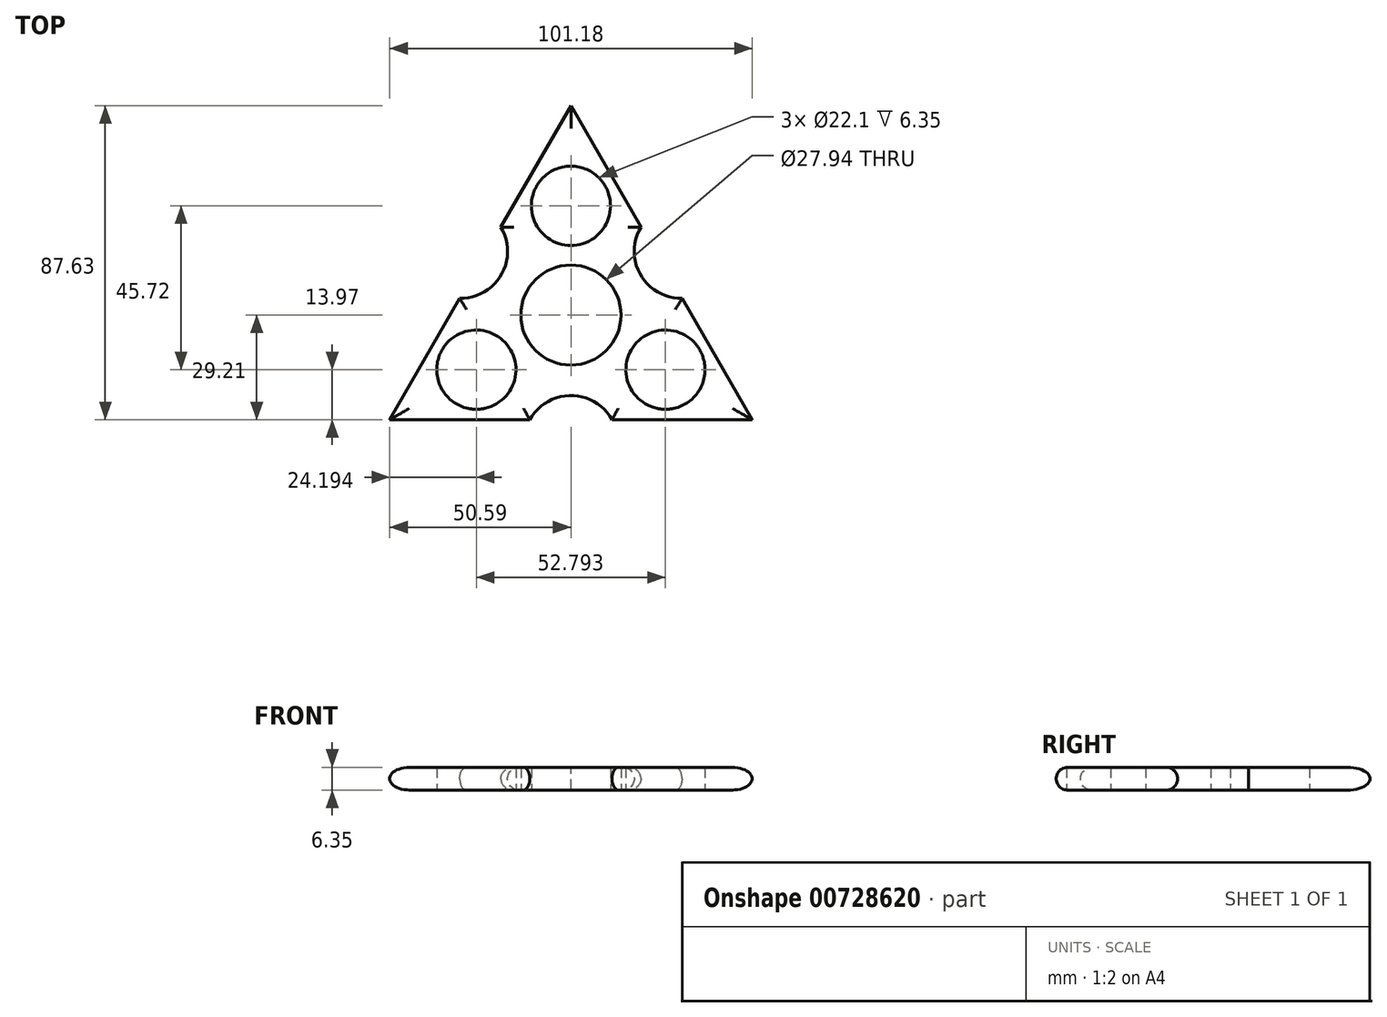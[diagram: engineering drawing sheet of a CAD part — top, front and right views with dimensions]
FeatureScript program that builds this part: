
annotation { "Feature Type Name" : "Feature", "Feature Type Description" : "" }
export const myFeature = defineFeature(function(context is Context, id is Id, definition is map)
    precondition{}
    {
        {
            var Q0;
            Q0=qCreatedBy(makeId("Top.planeOp"),FACE);
            var sketch = newSketch(context, id + "F0", { "sketchPlane" : qUnion([Q0])});
            skCircle(sketch, "E0", {"center": v(0, 0) * mm, "radius": 11.05 * mm});
            skCircle(sketch, "E1", {"center": v(0, 0) * mm, "radius": 13.97 * mm});
            skLineSegment(sketch, "E2", {"start": v(0, 0) * mm, "end": v(0, 30.48) * mm});
            skCircle(sketch, "E3", {"center": v(0, 30.48) * mm, "radius": 11.05 * mm});
            skCircle(sketch, "E4", {"center": v(0, 30.48) * mm, "radius": 13.97 * mm});
            skCircle(sketch, "E5.1.0", {"center": v(-26.4, -15.24) * mm, "radius": 11.05 * mm});
            skCircle(sketch, "E5.1.1", {"center": v(-26.4, -15.24) * mm, "radius": 13.97 * mm});
            skCircle(sketch, "E5.2.0", {"center": v(26.4, -15.24) * mm, "radius": 11.05 * mm});
            skCircle(sketch, "E5.2.1", {"center": v(26.4, -15.24) * mm, "radius": 13.97 * mm});
            skLineSegment(sketch, "E6", {"start": v(0, 30.48) * mm, "end": v(0, 58.42) * mm});
            skLineSegment(sketch, "E7", {"start": v(0, 58.42) * mm, "end": v(-19.57, 24.53) * mm});
            skLineSegment(sketch, "E8", {"start": v(-50.6, -29.2) * mm, "end": v(-11.46, -29.21) * mm});
            skLineSegment(sketch, "E9", {"start": v(0, 58.42) * mm, "end": v(19.57, 24.53) * mm});
            skLineSegment(sketch, "E10", {"start": v(-9.57, 5.52) * mm, "end": v(-12.1, 6.99) * mm});
            skArc(sketch, "E11", {"start": v(-31.03, 4.68) * mm, "mid": v(-19.43, 11.22) * mm, "end": v(-19.57, 24.53) * mm});
            skLineSegment(sketch, "E12.trimOffspring", {"start": v(-31.03, 4.68) * mm, "end": v(-50.6, -29.2) * mm});
            skArc(sketch, "E13.1.0", {"start": v(11.46, -29.21) * mm, "mid": v(0, -22.44) * mm, "end": v(-11.46, -29.21) * mm});
            skArc(sketch, "E13.2.0", {"start": v(19.57, 24.53) * mm, "mid": v(19.43, 11.22) * mm, "end": v(31.03, 4.68) * mm});
            skLineSegment(sketch, "E14.trimOffspring", {"start": v(31.03, 4.68) * mm, "end": v(50.6, -29.21) * mm});
            skLineSegment(sketch, "E15.trimOffspring", {"start": v(11.46, -29.21) * mm, "end": v(50.6, -29.21) * mm});
            skSolve(sketch);
        }
        {
            var Q0;
            Q0=qSketchRegion(id+"F0",true);
            extrude(context, id + "F1", {"entities" : qUnion([Q0]), "depth" : 6.35 * mm, "offsetDistance" : 25.4 * mm});
        }
        {
            var Q0;
            Q0=makeQuery(id+"F1.opExtrude","CAP_EDGE",EDGE,{"disambiguationData":[OSD([sQuery(id+"F0.wireOp",EDGE,"E7")])],"isStart":false});
            var Q1;
            Q1=makeQuery(id+"F1.opExtrude","CAP_EDGE",EDGE,{"disambiguationData":[OSD([sQuery(id+"F0.wireOp",EDGE,"E9")])],"isStart":false});
            var Q2;
            Q2=makeQuery(id+"F1.opExtrude","CAP_EDGE",EDGE,{"disambiguationData":[OSD([sQuery(id+"F0.wireOp",EDGE,"E13.2.0")])],"isStart":false});
            var Q3;
            Q3=makeQuery(id+"F1.opExtrude","CAP_EDGE",EDGE,{"disambiguationData":[OSD([sQuery(id+"F0.wireOp",EDGE,"E11")])],"isStart":false});
            var Q4;
            Q4=makeQuery(id+"F1.opExtrude","CAP_EDGE",EDGE,{"disambiguationData":[OSD([sQuery(id+"F0.wireOp",EDGE,"E12.trimOffspring")])],"isStart":false});
            var Q5;
            Q5=makeQuery(id+"F1.opExtrude","CAP_EDGE",EDGE,{"disambiguationData":[OSD([sQuery(id+"F0.wireOp",EDGE,"E8")])],"isStart":false});
            var Q6;
            Q6=makeQuery(id+"F1.opExtrude","CAP_EDGE",EDGE,{"disambiguationData":[OSD([sQuery(id+"F0.wireOp",EDGE,"E13.1.0")])],"isStart":false});
            var Q7;
            Q7=makeQuery(id+"F1.opExtrude","CAP_EDGE",EDGE,{"disambiguationData":[OSD([sQuery(id+"F0.wireOp",EDGE,"E15.trimOffspring")])],"isStart":false});
            var Q8;
            Q8=makeQuery(id+"F1.opExtrude","CAP_EDGE",EDGE,{"disambiguationData":[OSD([sQuery(id+"F0.wireOp",EDGE,"E14.trimOffspring")])],"isStart":false});
            var Q9;
            Q9=makeQuery(id+"F1.opExtrude","CAP_EDGE",EDGE,{"disambiguationData":[OSD([sQuery(id+"F0.wireOp",EDGE,"E9")])],"isStart":true});
            var Q10;
            Q10=makeQuery(id+"F1.opExtrude","CAP_EDGE",EDGE,{"disambiguationData":[OSD([sQuery(id+"F0.wireOp",EDGE,"E13.2.0")])],"isStart":true});
            var Q11;
            Q11=makeQuery(id+"F1.opExtrude","CAP_EDGE",EDGE,{"disambiguationData":[OSD([sQuery(id+"F0.wireOp",EDGE,"E14.trimOffspring")])],"isStart":true});
            var Q12;
            Q12=makeQuery(id+"F1.opExtrude","CAP_EDGE",EDGE,{"disambiguationData":[OSD([sQuery(id+"F0.wireOp",EDGE,"E15.trimOffspring")])],"isStart":true});
            var Q13;
            Q13=makeQuery(id+"F1.opExtrude","CAP_EDGE",EDGE,{"disambiguationData":[OSD([sQuery(id+"F0.wireOp",EDGE,"E13.1.0")])],"isStart":true});
            var Q14;
            Q14=makeQuery(id+"F1.opExtrude","CAP_EDGE",EDGE,{"disambiguationData":[OSD([sQuery(id+"F0.wireOp",EDGE,"E8")])],"isStart":true});
            var Q15;
            Q15=makeQuery(id+"F1.opExtrude","CAP_EDGE",EDGE,{"disambiguationData":[OSD([sQuery(id+"F0.wireOp",EDGE,"E12.trimOffspring")])],"isStart":true});
            var Q16;
            Q16=makeQuery(id+"F1.opExtrude","CAP_EDGE",EDGE,{"disambiguationData":[OSD([sQuery(id+"F0.wireOp",EDGE,"E11")])],"isStart":true});
            var Q17;
            Q17=makeQuery(id+"F1.opExtrude","CAP_EDGE",EDGE,{"disambiguationData":[OSD([sQuery(id+"F0.wireOp",EDGE,"E7")])],"isStart":true});
            fillet(context, id + "F2", {"entities" : qUnion([Q0, Q1, Q2, Q3, Q4, Q5, Q6, Q7, Q8, Q9, Q10, Q11, Q12, Q13, Q14, Q15, Q16, Q17]), "radius" : 3.17 * mm, "tangentPropagation" : true, "allowEdgeOverflow" : false});
        }
    });
